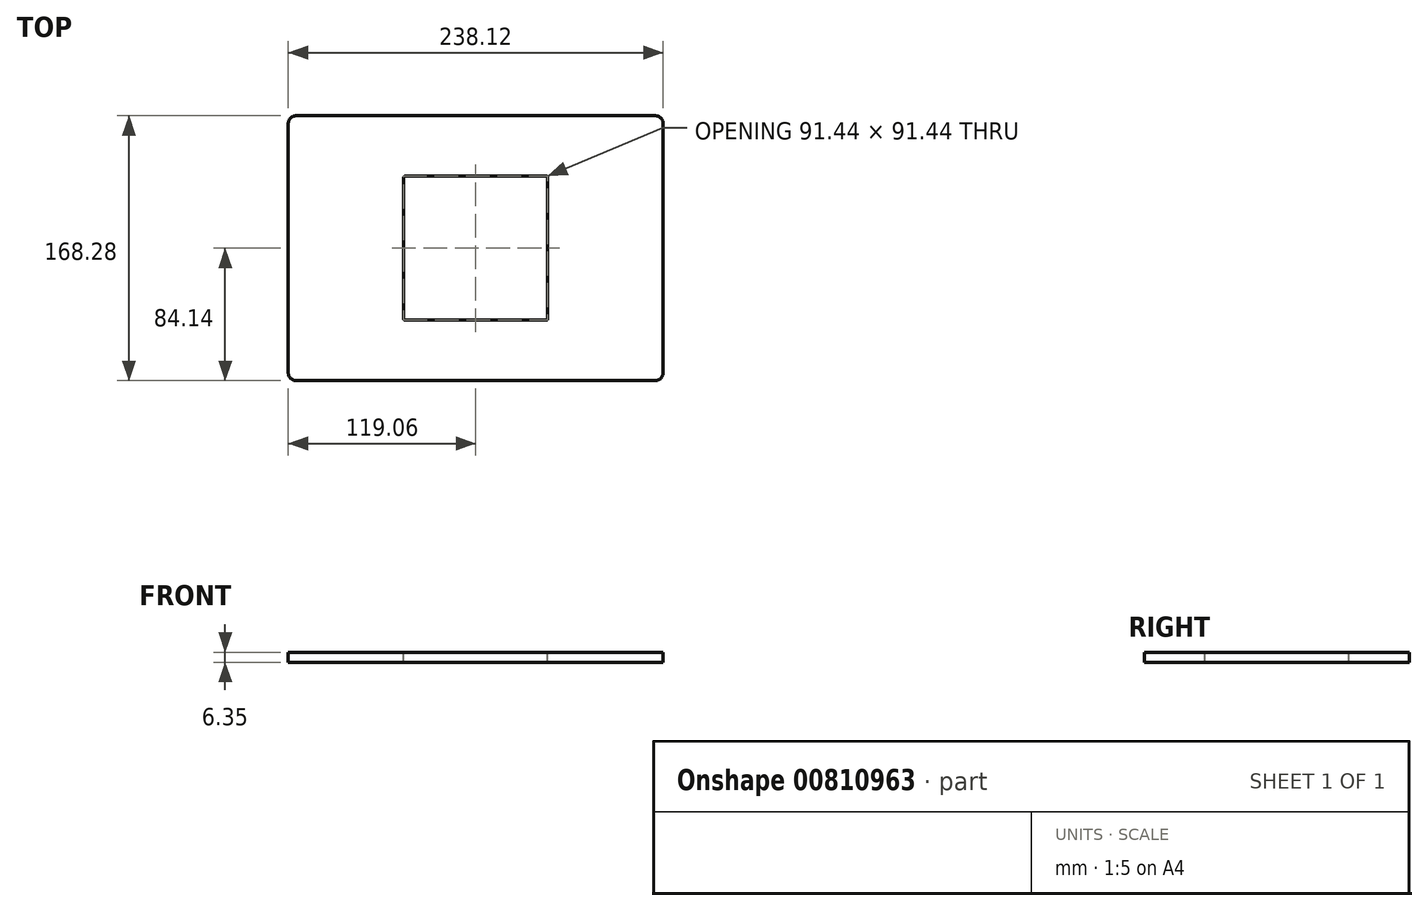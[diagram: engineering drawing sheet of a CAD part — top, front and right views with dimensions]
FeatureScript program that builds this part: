
annotation { "Feature Type Name" : "Feature", "Feature Type Description" : "" }
export const myFeature = defineFeature(function(context is Context, id is Id, definition is map)
    precondition{}
    {
        {
            var Q0;
            Q0=qCreatedBy(makeId("Top.planeOp"),FACE);
            var sketch = newSketch(context, id + "F0", { "sketchPlane" : qUnion([Q0])});
            skLineSegment(sketch, "E0.bottom", {"start": v(119.06, 84.14) * mm, "end": v(-119.06, 84.14) * mm});
            skLineSegment(sketch, "E0.top", {"start": v(119.06, -84.14) * mm, "end": v(-119.06, -84.14) * mm});
            skLineSegment(sketch, "E0.left", {"start": v(119.06, 84.14) * mm, "end": v(119.06, -84.14) * mm});
            skLineSegment(sketch, "E0.right", {"start": v(-119.06, 84.14) * mm, "end": v(-119.06, -84.14) * mm});
            skPoint(sketch, "E0.middle", {"position": v(0, 0) * mm});
            skSolve(sketch);
        }
        {
            var Q0;
            Q0 = qSketchRegion(id + "F0", true);
            extrude(context, id + "F1", {"entities" : qUnion([Q0]), "depth" : 6.35 * mm, "offsetDistance" : 25.4 * mm});
        }
        {
            var Q0;
            Q0=makeQuery(id+"F1.opExtrude","SWEPT_EDGE",EDGE,{"disambiguationData":[OSD([sQuery(id+"F0.wireOp",EDGE,"E0.bottom"),sQuery(id+"F0.wireOp",EDGE,"E0.left")])]});
            var Q1;
            Q1=makeQuery(id+"F1.opExtrude","SWEPT_EDGE",EDGE,{"disambiguationData":[OSD([sQuery(id+"F0.wireOp",EDGE,"E0.bottom"),sQuery(id+"F0.wireOp",EDGE,"E0.right")])]});
            var Q2;
            Q2=makeQuery(id+"F1.opExtrude","SWEPT_EDGE",EDGE,{"disambiguationData":[OSD([sQuery(id+"F0.wireOp",EDGE,"E0.top"),sQuery(id+"F0.wireOp",EDGE,"E0.left")])]});
            var Q3;
            Q3=makeQuery(id+"F1.opExtrude","SWEPT_EDGE",EDGE,{"disambiguationData":[OSD([sQuery(id+"F0.wireOp",EDGE,"E0.top"),sQuery(id+"F0.wireOp",EDGE,"E0.right")])]});
            fillet(context, id + "F2", {"entities" : qUnion([Q0, Q1, Q2, Q3]), "radius" : 5.08 * mm, "tangentPropagation" : true, "allowEdgeOverflow" : false});
        }
        {
            var Q0;
            Q0=makeQuery(id+"F1.opExtrude","CAP_FACE",FACE,{"disambiguationData":[OSD([sQuery(id+"F0.wireOp",EDGE,"E0.bottom"),sQuery(id+"F0.wireOp",EDGE,"E0.top"),sQuery(id+"F0.wireOp",EDGE,"E0.left"),sQuery(id+"F0.wireOp",EDGE,"E0.right")])],"isStart":false});
            var sketch = newSketch(context, id + "F3", { "sketchPlane" : qUnion([Q0])});
            skLineSegment(sketch, "E1.bottom", {"start": v(44.45, 44.45) * mm, "end": v(-44.45, 44.45) * mm});
            skLineSegment(sketch, "E1.top", {"start": v(44.45, -44.45) * mm, "end": v(-44.45, -44.45) * mm});
            skLineSegment(sketch, "E1.left", {"start": v(44.45, 44.45) * mm, "end": v(44.45, -44.45) * mm});
            skLineSegment(sketch, "E1.right", {"start": v(-44.45, 44.45) * mm, "end": v(-44.45, -44.45) * mm});
            skPoint(sketch, "E1.middle", {"position": v(0, 0) * mm});
            skSolve(sketch);
        }
        {
            var Q0;
            Q0 = qSketchRegion(id + "F3", true);
            extrude(context, id + "F4", {"entities" : qUnion([Q0]), "operationType" : NewBodyOperationType.REMOVE, "oppositeDirection" : true, "depth" : 25.4 * mm, "offsetDistance" : 25.4 * mm});
        }
        {
            var Q0;
            Q0=makeQuery(id+"F1.opExtrude","CAP_FACE",FACE,{"disambiguationData":[OSD([sQuery(id+"F0.wireOp",EDGE,"E0.bottom"),sQuery(id+"F0.wireOp",EDGE,"E0.top"),sQuery(id+"F0.wireOp",EDGE,"E0.left"),sQuery(id+"F0.wireOp",EDGE,"E0.right")])],"isStart":false});
            var sketch = newSketch(context, id + "F5", { "sketchPlane" : qUnion([Q0])});
            skLineSegment(sketch, "E2.0", {"start": v(44.93, 45.72) * mm, "end": v(-44.93, 45.72) * mm});
            skLineSegment(sketch, "E2.1", {"start": v(45.72, 44.93) * mm, "end": v(45.72, -44.93) * mm});
            skLineSegment(sketch, "E2.2", {"start": v(44.93, -45.72) * mm, "end": v(-44.93, -45.72) * mm});
            skLineSegment(sketch, "E2.3", {"start": v(-45.72, 44.93) * mm, "end": v(-45.72, -44.93) * mm});
            skPoint(sketch, "E3.visualSharp", {"position": v(-45.72, 45.72) * mm});
            skArc(sketch, "E3.filletArc", {"start": v(-44.93, 45.72) * mm, "mid": v(-45.49, 45.49) * mm, "end": v(-45.72, 44.93) * mm});
            skPoint(sketch, "E4.visualSharp", {"position": v(45.72, 45.72) * mm});
            skArc(sketch, "E4.filletArc", {"start": v(45.72, 44.93) * mm, "mid": v(45.49, 45.49) * mm, "end": v(44.93, 45.72) * mm});
            skPoint(sketch, "E5.visualSharp", {"position": v(45.72, -45.72) * mm});
            skArc(sketch, "E5.filletArc", {"start": v(44.93, -45.72) * mm, "mid": v(45.49, -45.49) * mm, "end": v(45.72, -44.93) * mm});
            skPoint(sketch, "E6.visualSharp", {"position": v(-45.72, -45.72) * mm});
            skArc(sketch, "E6.filletArc", {"start": v(-45.72, -44.93) * mm, "mid": v(-45.49, -45.49) * mm, "end": v(-44.93, -45.72) * mm});
            skSolve(sketch);
        }
        {
            var Q0;
            Q0 = qSketchRegion(id + "F5", true);
            extrude(context, id + "F6", {"entities" : qUnion([Q0]), "operationType" : NewBodyOperationType.REMOVE, "oppositeDirection" : true, "depth" : 25.4 * mm, "offsetDistance" : 25.4 * mm});
        }
    });
